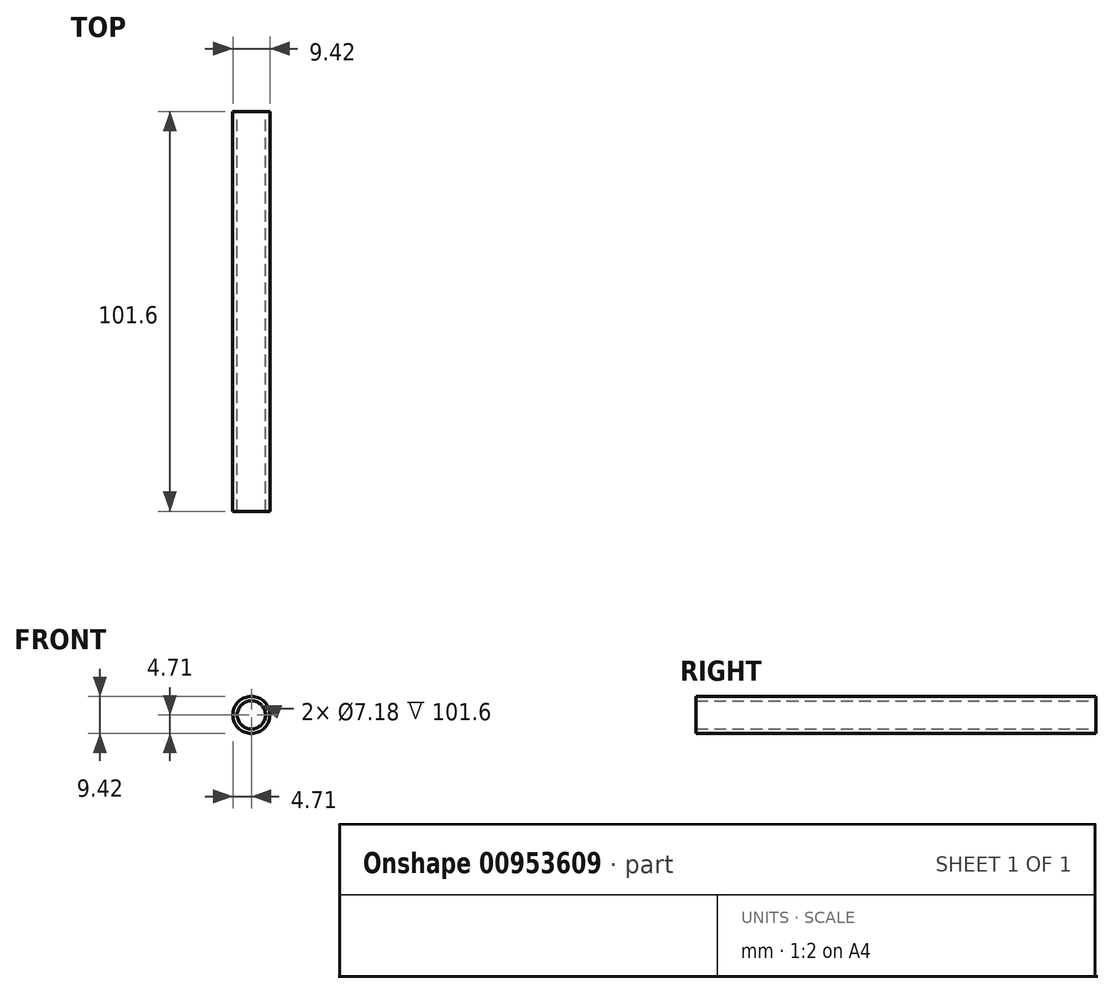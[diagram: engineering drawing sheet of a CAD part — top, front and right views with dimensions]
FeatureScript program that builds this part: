
annotation { "Feature Type Name" : "Feature", "Feature Type Description" : "" }
export const myFeature = defineFeature(function(context is Context, id is Id, definition is map)
    precondition{}
    {
        {
            var Q0;
            Q0=qCreatedBy(makeId("Front.planeOp"),FACE);
            var sketch = newSketch(context, id + "F0", { "sketchPlane" : qUnion([Q0])});
            skCircle(sketch, "E0", {"center": v(0, 0) * mm, "radius": 4.71 * mm});
            skCircle(sketch, "E1", {"center": v(0, 0) * mm, "radius": 3.59 * mm});
            skSolve(sketch);
        }
        {
            var Q0;
            Q0 = qSketchRegion(id + "F0", true);
            extrude(context, id + "F1", {"entities" : qUnion([Q0]), "depth" : 101.6 * mm, "offsetDistance" : 25.4 * mm});
        }
    });
